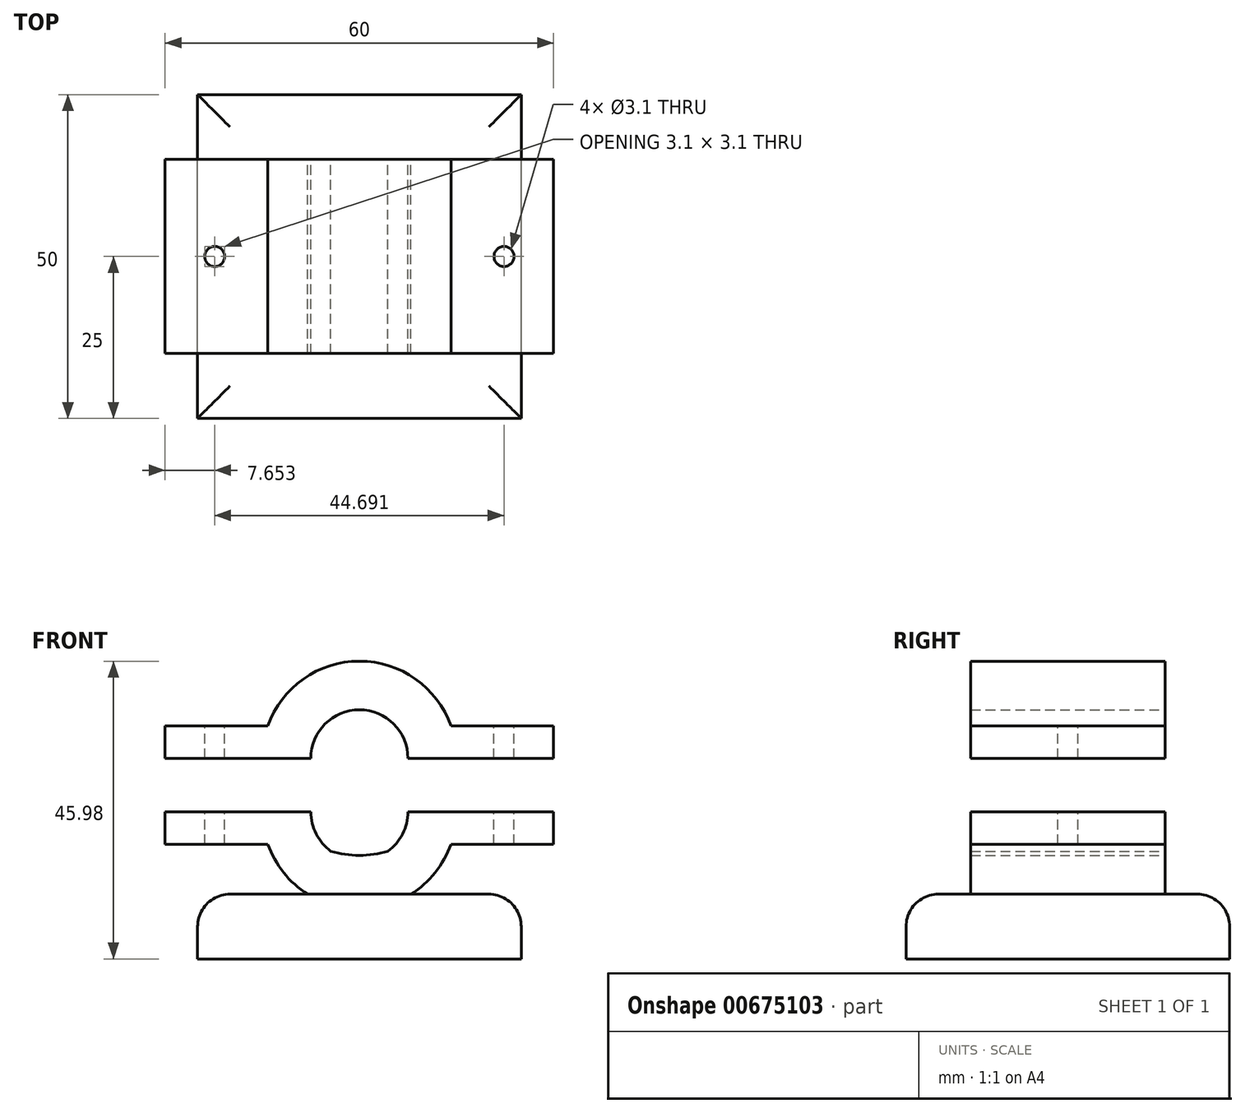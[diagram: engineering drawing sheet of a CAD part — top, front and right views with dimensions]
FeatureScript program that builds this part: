
annotation { "Feature Type Name" : "Feature", "Feature Type Description" : "" }
export const myFeature = defineFeature(function(context is Context, id is Id, definition is map)
    precondition{}
    {
        {
            var Q0;
            Q0=qCreatedBy(makeId("Top.planeOp"),FACE);
            var sketch = newSketch(context, id + "F0", { "sketchPlane" : qUnion([Q0])});
            skLineSegment(sketch, "E0.bottom", {"start": v(25, -25) * mm, "end": v(-25, -25) * mm});
            skLineSegment(sketch, "E0.top", {"start": v(25, 25) * mm, "end": v(-25, 25) * mm});
            skLineSegment(sketch, "E0.left", {"start": v(25, -25) * mm, "end": v(25, 25) * mm});
            skLineSegment(sketch, "E0.right", {"start": v(-25, -25) * mm, "end": v(-25, 25) * mm});
            skPoint(sketch, "E0.middle", {"position": v(0, 0) * mm});
            skSolve(sketch);
        }
        {
            var Q0;
            Q0=makeQuery(id+"F0.imprint","IMPRINT",FACE,{"disambiguationData":[TD([[makeQuery(id+"F0.imprint","IMPRINT",EDGE,{"derivedFrom":sQuery(id+"F0.wireOp",EDGE,"E0.bottom")}),-1.0]])]});
            extrude(context, id + "F1", {"entities" : qUnion([Q0]), "depth" : 10 * mm, "offsetDistance" : 25 * mm});
        }
        {
            var Q0;
            Q0=makeQuery(id+"F1.opExtrude","CAP_EDGE",EDGE,{"disambiguationData":[OSD([sQuery(id+"F0.wireOp",EDGE,"E0.bottom")])],"isStart":false});
            var Q1;
            Q1=makeQuery(id+"F1.opExtrude","CAP_EDGE",EDGE,{"disambiguationData":[OSD([sQuery(id+"F0.wireOp",EDGE,"E0.right")])],"isStart":false});
            var Q2;
            Q2=makeQuery(id+"F1.opExtrude","CAP_EDGE",EDGE,{"disambiguationData":[OSD([sQuery(id+"F0.wireOp",EDGE,"E0.left")])],"isStart":false});
            var Q3;
            Q3=makeQuery(id+"F1.opExtrude","CAP_EDGE",EDGE,{"disambiguationData":[OSD([sQuery(id+"F0.wireOp",EDGE,"E0.top")])],"isStart":false});
            fillet(context, id + "F2", {"entities" : qUnion([Q0, Q1, Q2, Q3]), "radius" : 5 * mm, "tangentPropagation" : true, "allowEdgeOverflow" : false});
        }
        {
            var Q0;
            Q0=qCreatedBy(makeId("Front.planeOp"),FACE);
            var sketch = newSketch(context, id + "F3", { "sketchPlane" : qUnion([Q0])});
            skArc(sketch, "E1", {"start": v(-14.14, 17.7) * mm, "mid": v(0, 7.7) * mm, "end": v(14.14, 17.7) * mm});
            skLineSegment(sketch, "E2", {"start": v(-7.5, 22.7) * mm, "end": v(-15, 22.7) * mm});
            skLineSegment(sketch, "E3", {"start": v(-15, 22.7) * mm, "end": v(-7.5, 22.7) * mm});
            skLineSegment(sketch, "E4", {"start": v(-7.5, 22.7) * mm, "end": v(-30, 22.7) * mm});
            skLineSegment(sketch, "E5", {"start": v(-30, 22.7) * mm, "end": v(-15, 22.7) * mm});
            skLineSegment(sketch, "E6", {"start": v(15, 22.7) * mm, "end": v(30, 22.7) * mm});
            skArc(sketch, "E7", {"start": v(-7.5, 22.7) * mm, "mid": v(-6.68, 19.3) * mm, "end": v(-4.41, 16.64) * mm});
            skLineSegment(sketch, "E8.bottom", {"start": v(-30, 22.7) * mm, "end": v(-14.14, 22.7) * mm});
            skLineSegment(sketch, "E8.top", {"start": v(-30, 17.7) * mm, "end": v(-14.14, 17.7) * mm});
            skLineSegment(sketch, "E8.left", {"start": v(-30, 22.7) * mm, "end": v(-30, 17.7) * mm});
            skLineSegment(sketch, "E9.bottom", {"start": v(30, 22.7) * mm, "end": v(14.14, 22.7) * mm});
            skLineSegment(sketch, "E9.top", {"start": v(30, 17.7) * mm, "end": v(14.14, 17.7) * mm});
            skLineSegment(sketch, "E9.left", {"start": v(30, 22.7) * mm, "end": v(30, 17.7) * mm});
            skLineSegment(sketch, "E10.trimOffspring", {"start": v(7.5, 22.7) * mm, "end": v(15, 22.7) * mm});
            skArc(sketch, "E11", {"start": v(7.5, 30.98) * mm, "mid": v(0, 38.48) * mm, "end": v(-7.5, 30.98) * mm});
            skArc(sketch, "E12", {"start": v(-4.41, 16.64) * mm, "mid": v(0, 15.98) * mm, "end": v(4.41, 16.64) * mm});
            skLineSegment(sketch, "E13", {"start": v(-7.5, 30.98) * mm, "end": v(-15, 30.98) * mm});
            skLineSegment(sketch, "E14", {"start": v(7.5, 30.98) * mm, "end": v(15, 30.98) * mm});
            skLineSegment(sketch, "E15", {"start": v(15, 30.98) * mm, "end": v(30, 30.98) * mm});
            skLineSegment(sketch, "E16", {"start": v(-15, 30.98) * mm, "end": v(-30, 30.98) * mm});
            skLineSegment(sketch, "E17.bottom", {"start": v(-30, 30.98) * mm, "end": v(-14.14, 30.98) * mm});
            skLineSegment(sketch, "E17.top", {"start": v(-30, 35.98) * mm, "end": v(-14.14, 35.98) * mm});
            skLineSegment(sketch, "E17.left", {"start": v(-30, 30.98) * mm, "end": v(-30, 35.98) * mm});
            skLineSegment(sketch, "E18.bottom", {"start": v(30, 30.98) * mm, "end": v(14.14, 30.98) * mm});
            skLineSegment(sketch, "E18.top", {"start": v(30, 35.98) * mm, "end": v(14.14, 35.98) * mm});
            skLineSegment(sketch, "E18.left", {"start": v(30, 30.98) * mm, "end": v(30, 35.98) * mm});
            skArc(sketch, "E19.trimOffspring", {"start": v(4.41, 16.64) * mm, "mid": v(6.68, 19.3) * mm, "end": v(7.5, 22.7) * mm});
            skArc(sketch, "E20.trimOffspring", {"start": v(14.14, 35.98) * mm, "mid": v(0, 45.98) * mm, "end": v(-14.14, 35.98) * mm});
            skSolve(sketch);
        }
        {
            var Q0;
            Q0=makeQuery(id+"F3.imprint","IMPRINT",FACE,{"disambiguationData":[TD([[makeQuery(id+"F3.imprint","IMPRINT",EDGE,{"derivedFrom":sQuery(id+"F3.wireOp",EDGE,"E11")}),-1.0]])]});
            var Q1;
            Q1=makeQuery(id+"F3.imprint","IMPRINT",FACE,{"disambiguationData":[TD([[makeQuery(id+"F3.imprint","IMPRINT",EDGE,{"derivedFrom":sQuery(id+"F3.wireOp",EDGE,"E1")}),1.0]])]});
            extrude(context, id + "F4", {"entities" : qUnion([Q0, Q1]), "operationType" : NewBodyOperationType.ADD, "depth" : 15 * mm, "offsetDistance" : 25 * mm, "hasSecondDirection" : true, "secondDirectionOppositeDirection" : true, "secondDirectionDepth" : 15 * mm});
        }
        {
            var Q0;
            Q0=makeQuery(id+"F4.opExtrude","SWEPT_FACE",FACE,{"disambiguationData":[OSD([sQuery(id+"F3.wireOp",EDGE,"E17.top")])]});
            var sketch = newSketch(context, id + "F5", { "sketchPlane" : qUnion([Q0])});
            skCircle(sketch, "E21", {"center": v(-22.35, 0) * mm, "radius": 1.55 * mm});
            skCircle(sketch, "E22", {"center": v(22.34, 0) * mm, "radius": 1.55 * mm});
            skSolve(sketch);
        }
        {
            var Q0;
            Q0 = qSketchRegion(id + "F5", true);
            extrude(context, id + "F6", {"entities" : qUnion([Q0]), "operationType" : NewBodyOperationType.REMOVE, "oppositeDirection" : true, "depth" : 25 * mm, "offsetDistance" : 25 * mm});
        }
    });
